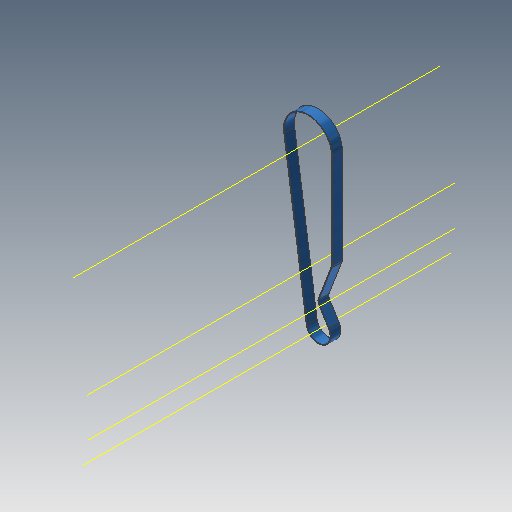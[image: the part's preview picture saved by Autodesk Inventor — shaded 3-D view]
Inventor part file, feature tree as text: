
AUTODESK INVENTOR PART (.ipt)
format: ipt  version: 2019.4 (Build 234330000, 330)  size: 115,712 bytes
history: native  units: mm (DEFAULTED — no unit token found)
features: other x9, sweep x1
ambient origin geometry x8: Origin, YZ Plane, XZ Plane, XY Plane, X Axis, Y Axis, Z Axis, Center Point
bodies: Solid1 (feature_tree)
feature tree (10):
  other  "スケッチ パス"
  other  "断面平面"
  other  "作業軸1"
  other  "作業軸2"
  other  "作業軸3"
  other  "作業軸4"
  other  "作業平面2"
  other  "作業平面3"
  other  "作業平面4"
  sweep  "ベルト"
